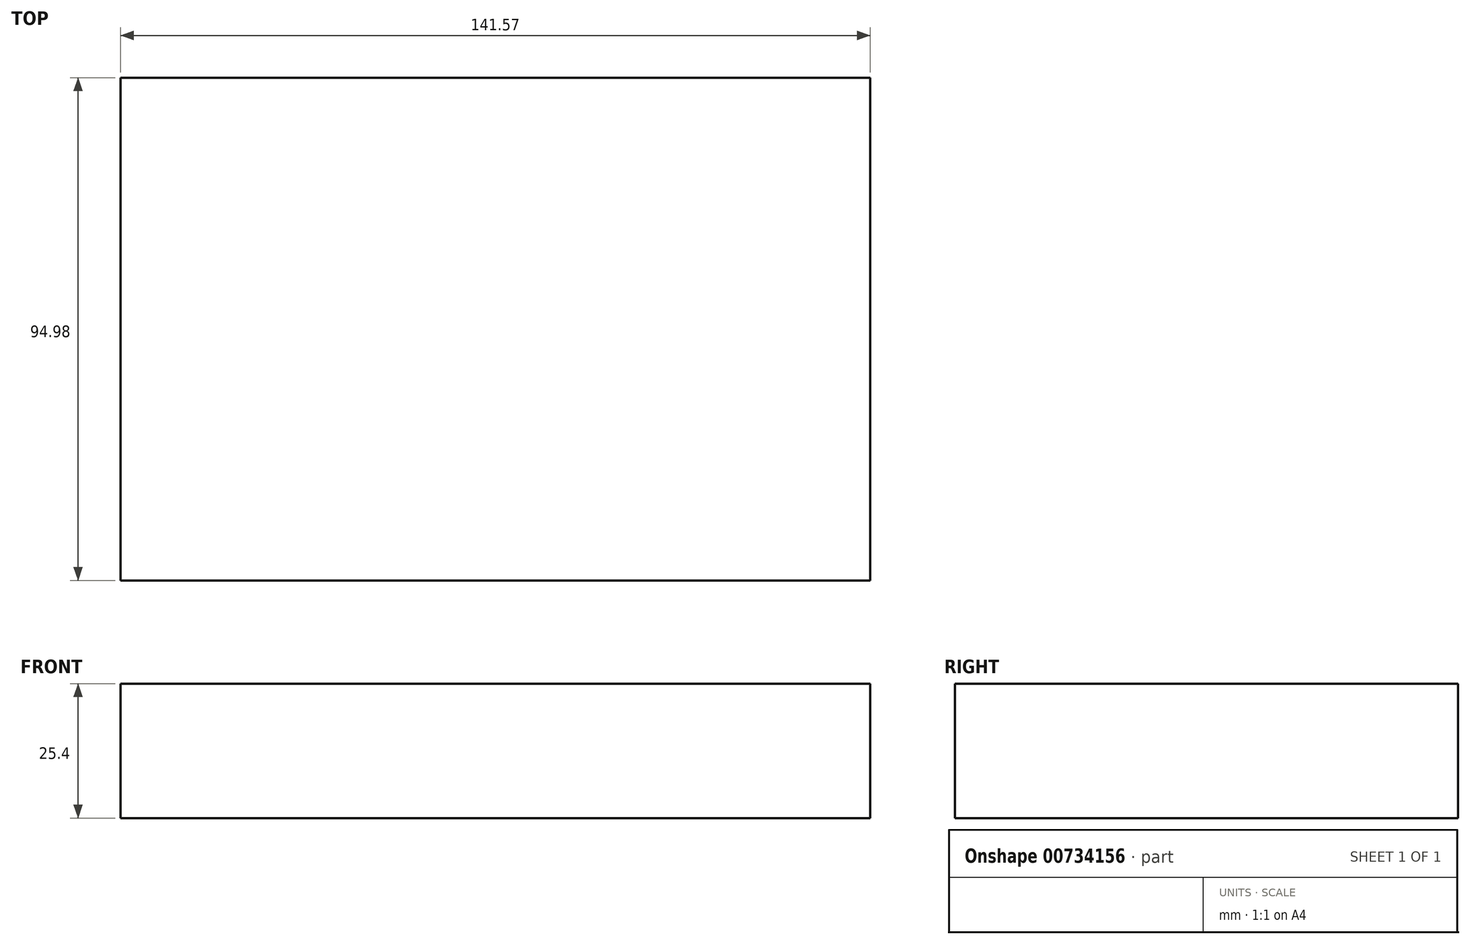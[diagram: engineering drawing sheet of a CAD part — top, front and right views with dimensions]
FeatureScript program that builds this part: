
annotation { "Feature Type Name" : "Feature", "Feature Type Description" : "" }
export const myFeature = defineFeature(function(context is Context, id is Id, definition is map)
    precondition{}
    {
        {
            var Q0;
            Q0=qCreatedBy(makeId("Top.planeOp"),FACE);
            var sketch = newSketch(context, id + "F0", { "sketchPlane" : qUnion([Q0])});
            skLineSegment(sketch, "E0.bottom", {"start": v(-49.56, 47.82) * mm, "end": v(92.01, 47.82) * mm});
            skLineSegment(sketch, "E0.top", {"start": v(-49.56, -47.16) * mm, "end": v(92.01, -47.16) * mm});
            skLineSegment(sketch, "E0.left", {"start": v(-49.56, 47.82) * mm, "end": v(-49.56, -47.16) * mm});
            skLineSegment(sketch, "E0.right", {"start": v(92.01, 47.82) * mm, "end": v(92.01, -47.16) * mm});
            skSolve(sketch);
        }
        {
            var Q0;
            Q0 = qSketchRegion(id + "F0", true);
            var Q1;
            Q1=makeQuery(id+"F0.imprint","IMPRINT",FACE,{"disambiguationData":[TD([[makeQuery(id+"F0.imprint","IMPRINT",EDGE,{"derivedFrom":sQuery(id+"F0.wireOp",EDGE,"E0.bottom")}),-1.0]])]});
            extrude(context, id + "F1", {"entities" : qUnion([Q0, Q1]), "depth" : 25.4 * mm, "offsetDistance" : 25.4 * mm});
        }
    });
